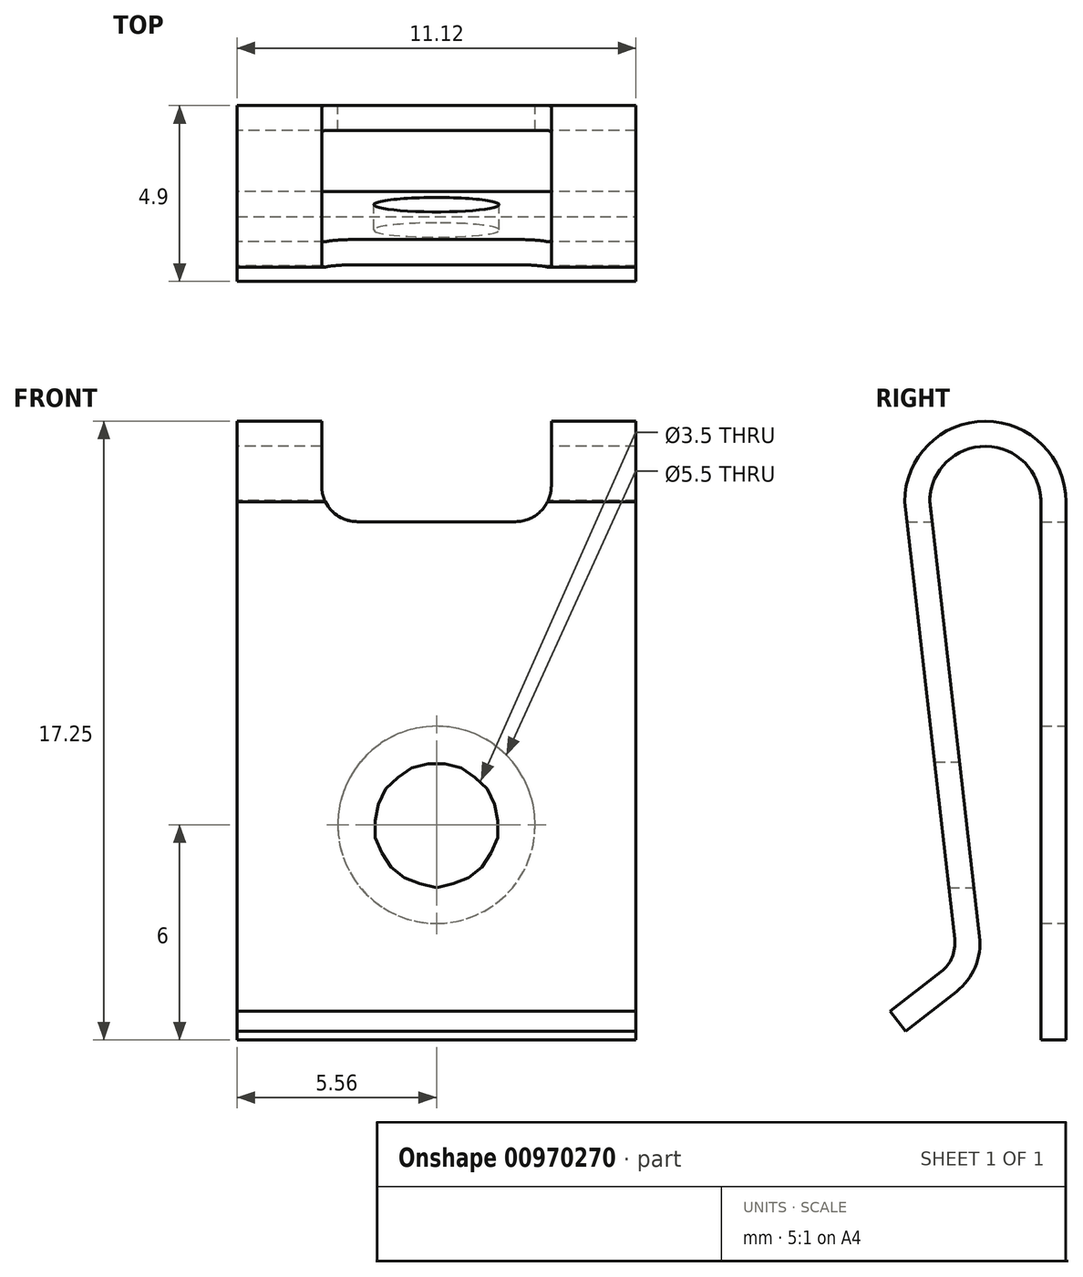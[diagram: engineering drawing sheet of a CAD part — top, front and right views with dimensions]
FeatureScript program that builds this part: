
annotation { "Feature Type Name" : "Feature", "Feature Type Description" : "" }
export const myFeature = defineFeature(function(context is Context, id is Id, definition is map)
    precondition{}
    {
        {
            var Q0;
            Q0=qCreatedBy(makeId("Right.planeOp"),FACE);
            var sketch = newSketch(context, id + "F0", { "sketchPlane" : qUnion([Q0])});
            skLineSegment(sketch, "E0", {"start": v(2.25, -15) * mm, "end": v(2.25, 0) * mm});
            skLineSegment(sketch, "E1", {"start": v(2.25, 0) * mm, "end": v(-2.25, 0) * mm, "construction": true});
            skLineSegment(sketch, "E2", {"start": v(-2.25, 0) * mm, "end": v(-0.8, -12.75) * mm});
            skLineSegment(sketch, "E3", {"start": v(-0.8, -12.75) * mm, "end": v(-2.65, -14.2) * mm});
            skArc(sketch, "E4", {"start": v(2.25, 0) * mm, "mid": v(0, 2.25) * mm, "end": v(-2.25, 0) * mm});
            skLineSegment(sketch, "E5.0", {"start": v(-0.05, -13.06) * mm, "end": v(-2.22, -14.75) * mm});
            skLineSegment(sketch, "E5.1", {"start": v(-1.55, 0.04) * mm, "end": v(-0.05, -13.06) * mm});
            skArc(sketch, "E5.2", {"start": v(1.55, 0) * mm, "mid": v(0.02, 1.55) * mm, "end": v(-1.55, 0.04) * mm});
            skLineSegment(sketch, "E5.3", {"start": v(1.55, -15) * mm, "end": v(1.55, 0) * mm});
            skLineSegment(sketch, "E6", {"start": v(-2.22, -14.75) * mm, "end": v(-2.65, -14.2) * mm});
            skLineSegment(sketch, "E7", {"start": v(2.25, -15) * mm, "end": v(1.55, -15) * mm});
            skSolve(sketch);
        }
        {
            var Q0;
            Q0=makeQuery(id+"F0.imprint","IMPRINT",FACE,{"disambiguationData":[TD([[makeQuery(id+"F0.imprint","IMPRINT",EDGE,{"derivedFrom":sQuery(id+"F0.wireOp",EDGE,"E0")}),1.0]])]});
            extrude(context, id + "F1", {"entities" : qUnion([Q0]), "endBound" : BoundingType.SYMMETRIC, "depth" : 11.12 * mm});
        }
        {
            var Q0;
            Q0=makeQuery(id+"F1.opExtrude","SWEPT_FACE",FACE,{"disambiguationData":[OSD([sQuery(id+"F0.wireOp",EDGE,"E0")])]});
            var sketch = newSketch(context, id + "F2", { "sketchPlane" : qUnion([Q0])});
            skLineSegment(sketch, "E8", {"start": v(0, -15) * mm, "end": v(0, -9) * mm, "construction": true});
            skCircle(sketch, "E9", {"center": v(0, -9) * mm, "radius": 2.75 * mm});
            skCircle(sketch, "E10", {"center": v(0, -9) * mm, "radius": 1.75 * mm});
            skLineSegment(sketch, "E11.bottom", {"start": v(-3.2, 3.95) * mm, "end": v(3.2, 3.95) * mm});
            skLineSegment(sketch, "E11.top", {"start": v(-3.2, -0.55) * mm, "end": v(3.2, -0.55) * mm});
            skLineSegment(sketch, "E11.left", {"start": v(-3.2, 3.95) * mm, "end": v(-3.2, -0.55) * mm});
            skLineSegment(sketch, "E11.right", {"start": v(3.2, 3.95) * mm, "end": v(3.2, -0.55) * mm});
            skSolve(sketch);
        }
        {
            var Q0;
            {var subQ0=sQuery(id+"F2.wireOp",EDGE,"E11.bottom");Q0=makeQuery(id+"F2.imprint","IMPRINT",FACE,{"disambiguationData":[TD([[makeQuery(id+"F2.imprint","IMPRINT",EDGE,{"derivedFrom":subQ0}),-1.0]])]});}
            var Q1;
            {var subQ0=sQuery(id+"F2.wireOp",EDGE,"E11.top");Q1=makeQuery(id+"F2.imprint","IMPRINT",FACE,{"disambiguationData":[TD([[makeQuery(id+"F2.imprint","IMPRINT",EDGE,{"derivedFrom":subQ0}),1.0]])]});}
            var Q2;
            Q2=makeQuery(id+"F2.imprint","IMPRINT",FACE,{"disambiguationData":[TD([[makeQuery(id+"F2.imprint","IMPRINT",EDGE,{"derivedFrom":sQuery(id+"F2.wireOp",EDGE,"E10")}),1.0]])]});
            extrude(context, id + "F3", {"entities" : qUnion([Q0, Q1, Q2]), "operationType" : NewBodyOperationType.REMOVE, "endBound" : BoundingType.THROUGH_ALL, "oppositeDirection" : true, "depth" : 25 * mm});
        }
        {
            var Q0;
            Q0=makeQuery(id+"F2.imprint","IMPRINT",FACE,{"disambiguationData":[TD([[makeQuery(id+"F2.imprint","IMPRINT",EDGE,{"derivedFrom":sQuery(id+"F2.wireOp",EDGE,"E9")}),1.0]])]});
            var Q1;
            Q1=makeQuery(id+"F1.opExtrude","SWEPT_FACE",FACE,{"disambiguationData":[OSD([sQuery(id+"F0.wireOp",EDGE,"E5.3")])]});
            extrude(context, id + "F4", {"entities" : qUnion([Q0]), "operationType" : NewBodyOperationType.REMOVE, "endBound" : BoundingType.UP_TO_SURFACE, "oppositeDirection" : true, "endBoundEntityFace" : qUnion([Q1]), "depth" : 25 * mm});
        }
        {
            var Q0;
            Q0=makeQuery(id+"F3.boolean.opBoolean","COPY",EDGE,{"disambiguationData":[OD(0.0)],"derivedFrom":makeQuery(id+"F3.opExtrude","SWEPT_EDGE",EDGE,{"disambiguationData":[OSD([sQuery(id+"F2.wireOp",EDGE,"E11.top"),sQuery(id+"F2.wireOp",EDGE,"E11.right")])]})});
            var Q1;
            Q1=makeQuery(id+"F3.boolean.opBoolean","COPY",EDGE,{"disambiguationData":[OD(1.0)],"derivedFrom":makeQuery(id+"F3.opExtrude","SWEPT_EDGE",EDGE,{"disambiguationData":[OSD([sQuery(id+"F2.wireOp",EDGE,"E11.top"),sQuery(id+"F2.wireOp",EDGE,"E11.right")])]})});
            var Q2;
            Q2=makeQuery(id+"F3.boolean.opBoolean","COPY",EDGE,{"disambiguationData":[OD(0.0)],"derivedFrom":makeQuery(id+"F3.opExtrude","SWEPT_EDGE",EDGE,{"disambiguationData":[OSD([sQuery(id+"F2.wireOp",EDGE,"E11.top"),sQuery(id+"F2.wireOp",EDGE,"E11.left")])]})});
            var Q3;
            Q3=makeQuery(id+"F3.boolean.opBoolean","COPY",EDGE,{"disambiguationData":[OD(1.0)],"derivedFrom":makeQuery(id+"F3.opExtrude","SWEPT_EDGE",EDGE,{"disambiguationData":[OSD([sQuery(id+"F2.wireOp",EDGE,"E11.top"),sQuery(id+"F2.wireOp",EDGE,"E11.left")])]})});
            var Q4;
            Q4=makeQuery(id+"F1.opExtrude","SWEPT_EDGE",EDGE,{"disambiguationData":[OSD([sQuery(id+"F0.wireOp",EDGE,"E2"),sQuery(id+"F0.wireOp",EDGE,"E3")])]});
            fillet(context, id + "F5", {"entities" : qUnion([Q0, Q1, Q2, Q3, Q4]), "radius" : 1 * mm, "tangentPropagation" : true, "conicFillet" : false});
        }
        {
            var Q0;
            Q0=makeQuery(id+"F1.opExtrude","SWEPT_EDGE",EDGE,{"disambiguationData":[OSD([sQuery(id+"F0.wireOp",EDGE,"E5.0"),sQuery(id+"F0.wireOp",EDGE,"E5.1")])]});
            fillet(context, id + "F6", {"entities" : qUnion([Q0]), "radius" : 1.7 * mm, "tangentPropagation" : true, "conicFillet" : false});
        }
    });
